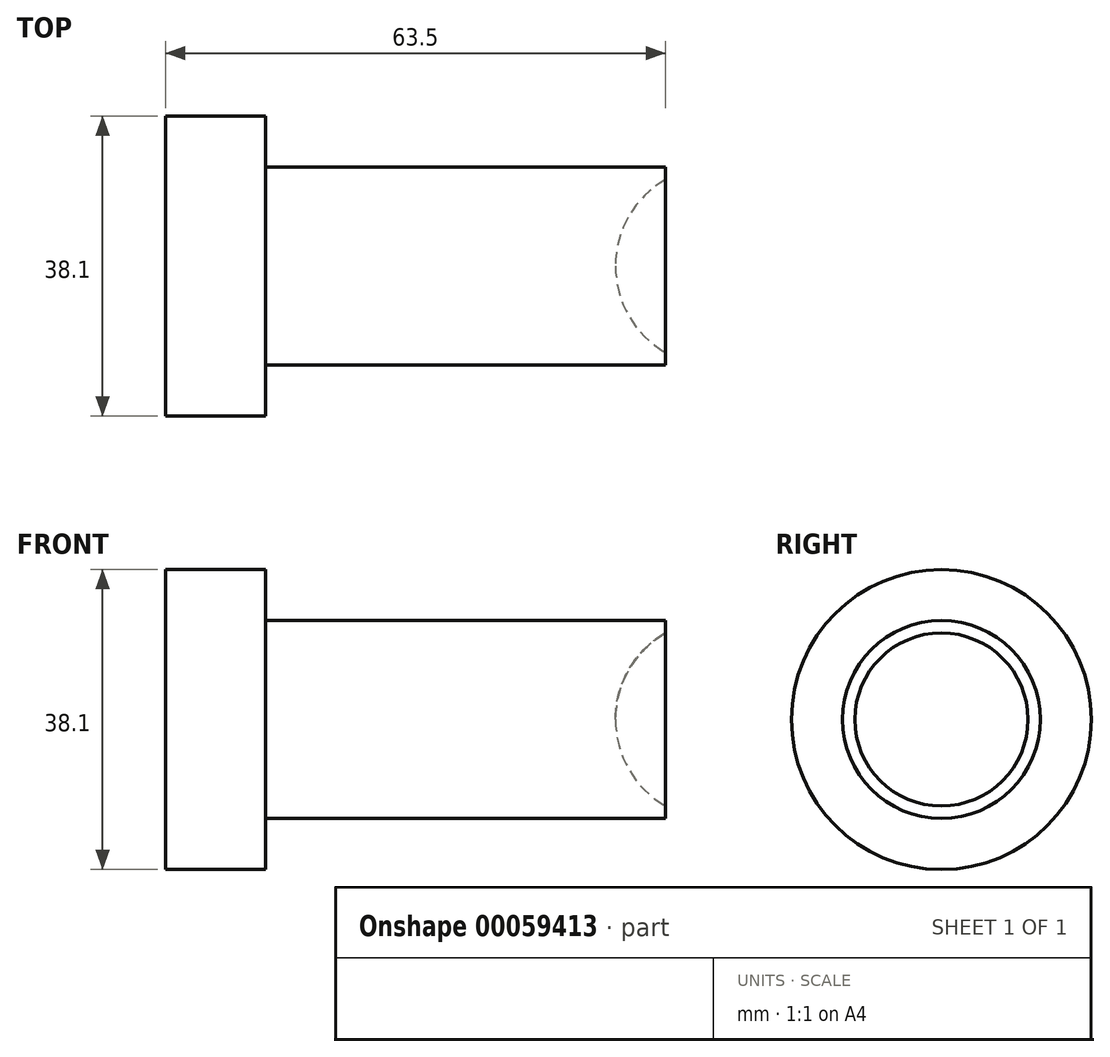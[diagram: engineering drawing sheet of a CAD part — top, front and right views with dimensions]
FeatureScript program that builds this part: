
annotation { "Feature Type Name" : "Feature", "Feature Type Description" : "" }
export const myFeature = defineFeature(function(context is Context, id is Id, definition is map)
    precondition{}
    {
        {
            var Q0;
            Q0=qCreatedBy(makeId("Front.planeOp"),FACE);
            var sketch = newSketch(context, id + "F0", { "sketchPlane" : qUnion([Q0])});
            skLineSegment(sketch, "E0", {"start": v(11.8, 4.29) * mm, "end": v(11.8, 23.34) * mm});
            skLineSegment(sketch, "E1", {"start": v(11.8, 23.34) * mm, "end": v(24.5, 23.34) * mm});
            skLineSegment(sketch, "E2", {"start": v(24.5, 23.34) * mm, "end": v(24.5, 16.86) * mm});
            skLineSegment(sketch, "E3", {"start": v(24.5, 16.86) * mm, "end": v(75.3, 16.86) * mm});
            skLineSegment(sketch, "E4", {"start": v(75.3, 16.86) * mm, "end": v(75.3, 15.29) * mm});
            skLineSegment(sketch, "E5", {"start": v(68.95, 4.29) * mm, "end": v(11.8, 4.29) * mm});
            skPoint(sketch, "E6.endSnap0", {"position": v(75.3, 10.57) * mm});
            skPoint(sketch, "E7.orphan", {"position": v(75.3, -13.3) * mm});
            skPoint(sketch, "E8.orphan", {"position": v(75.3, 4.29) * mm});
            skArc(sketch, "E9", {"start": v(75.3, 15.29) * mm, "mid": v(70.65, 10.64) * mm, "end": v(68.95, 4.29) * mm});
            skSolve(sketch);
        }
        {
            var Q0;
            Q0 = qSketchRegion(id + "F0", true);
            var Q1;
            Q1=sQuery(id+"F0.wireOp",EDGE,"E5");
            revolve(context, id + "F1", {"entities" : qUnion([Q0]), "axis" : qUnion([Q1]), "revolveType" : RevolveType.FULL});
        }
    });
